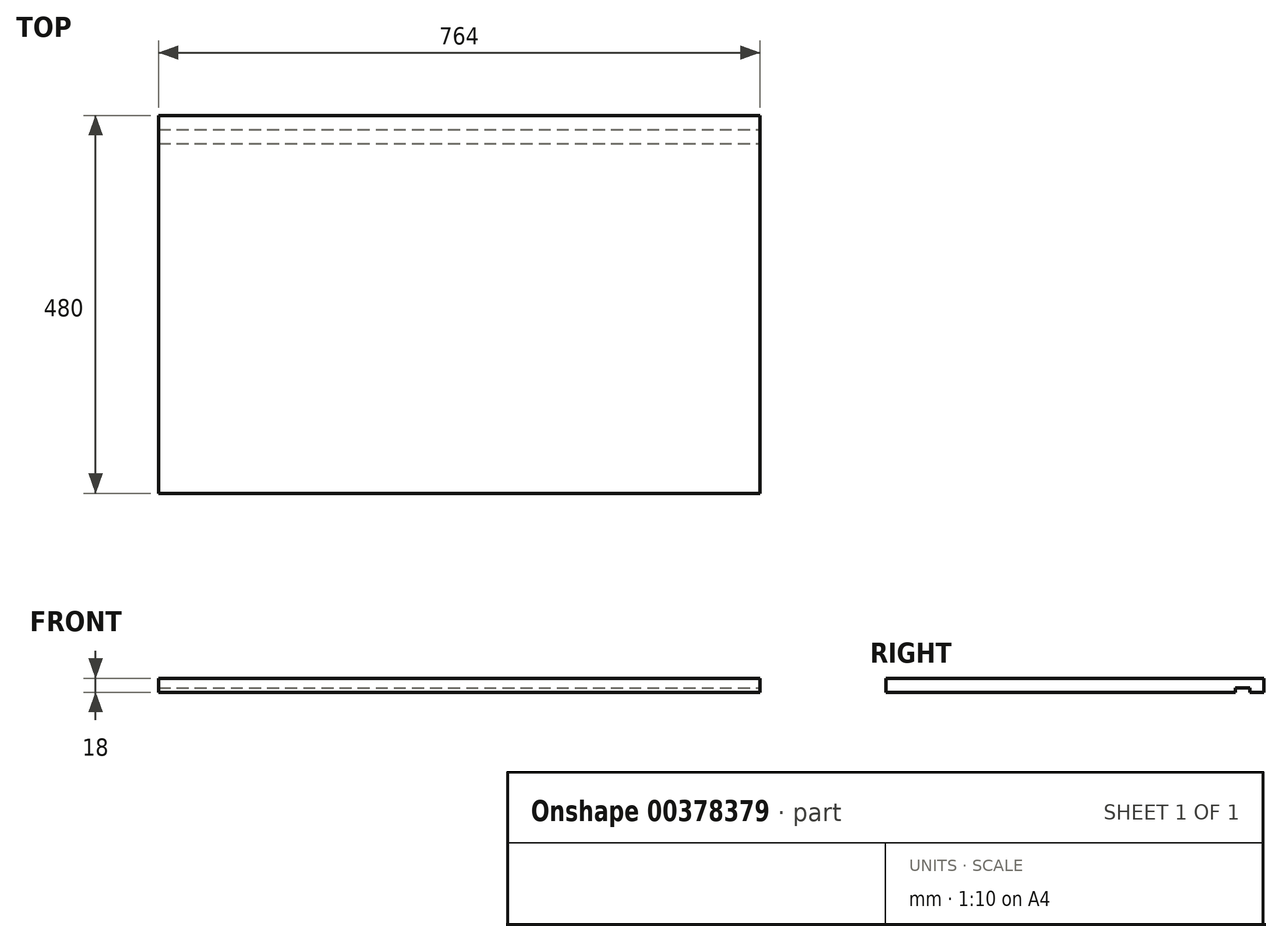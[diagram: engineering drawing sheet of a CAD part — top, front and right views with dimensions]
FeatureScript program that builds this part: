
annotation { "Feature Type Name" : "Feature", "Feature Type Description" : "" }
export const myFeature = defineFeature(function(context is Context, id is Id, definition is map)
    precondition{}
    {
        {
            var Q0;
            Q0=qCreatedBy(makeId("Top.planeOp"),FACE);
            var sketch = newSketch(context, id + "F0", { "sketchPlane" : qUnion([Q0])});
            skLineSegment(sketch, "E0.bottom", {"start": v(382, 240) * mm, "end": v(-382, 240) * mm});
            skLineSegment(sketch, "E0.top", {"start": v(382, -240) * mm, "end": v(-382, -240) * mm});
            skLineSegment(sketch, "E0.right", {"start": v(-382, 240) * mm, "end": v(-382, -240) * mm});
            skPoint(sketch, "E0.middle", {"position": v(0, 0) * mm});
            skLineSegment(sketch, "E1", {"start": v(382, -240) * mm, "end": v(382, 240) * mm});
            skSolve(sketch);
        }
        {
            var Q0;
            Q0=qSketchRegion(id+"F0",true);
            extrude(context, id + "F1", {"entities" : qUnion([Q0]), "depth" : 18 * mm});
        }
        {
            var Q0;
            Q0=makeQuery(id+"F1.opExtrude","CAP_FACE",FACE,{"disambiguationData":[OSD([sQuery(id+"F0.wireOp",EDGE,"E0.bottom"),sQuery(id+"F0.wireOp",EDGE,"E0.top"),sQuery(id+"F0.wireOp",EDGE,"E0.right"),sQuery(id+"F0.wireOp",EDGE,"E1")])],"isStart":true});
            var sketch = newSketch(context, id + "F2", { "sketchPlane" : qUnion([Q0])});
            skLineSegment(sketch, "E2.bottom", {"start": v(-382, -204) * mm, "end": v(555.34, -204) * mm});
            skLineSegment(sketch, "E2.top", {"start": v(-382, -222) * mm, "end": v(555.34, -222) * mm});
            skLineSegment(sketch, "E2.left", {"start": v(-382, -204) * mm, "end": v(-382, -222) * mm});
            skLineSegment(sketch, "E2.right", {"start": v(555.34, -204) * mm, "end": v(555.34, -222) * mm});
            skSolve(sketch);
        }
        {
            var Q0;
            Q0=qSketchRegion(id+"F2",true);
            extrude(context, id + "F3", {"entities" : qUnion([Q0]), "operationType" : NewBodyOperationType.REMOVE, "oppositeDirection" : true, "depth" : 6 * mm});
        }
    });
